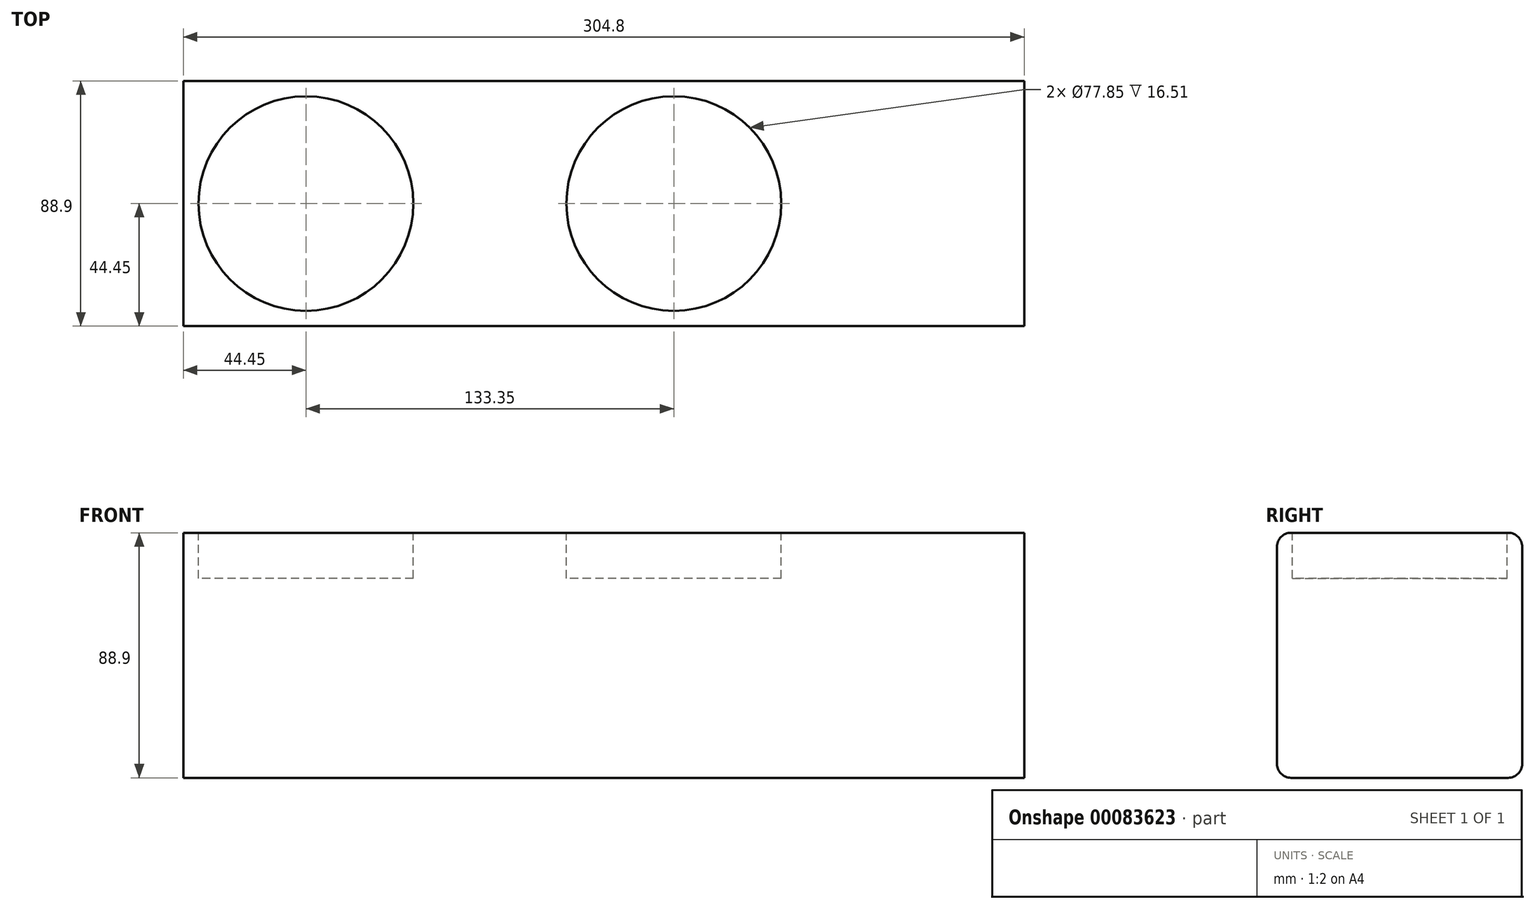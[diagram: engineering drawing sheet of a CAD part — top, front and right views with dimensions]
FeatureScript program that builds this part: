
annotation { "Feature Type Name" : "Feature", "Feature Type Description" : "" }
export const myFeature = defineFeature(function(context is Context, id is Id, definition is map)
    precondition{}
    {
        {
            var Q0;
            Q0=qCreatedBy(makeId("Right.planeOp"),FACE);
            var sketch = newSketch(context, id + "F0", { "sketchPlane" : qUnion([Q0])});
            skLineSegment(sketch, "E0.bottom", {"start": v(44.45, -44.45) * mm, "end": v(-44.45, -44.45) * mm});
            skLineSegment(sketch, "E0.top", {"start": v(44.45, 44.45) * mm, "end": v(-44.45, 44.45) * mm});
            skLineSegment(sketch, "E0.left", {"start": v(44.45, -44.45) * mm, "end": v(44.45, 44.45) * mm});
            skLineSegment(sketch, "E0.right", {"start": v(-44.45, -44.45) * mm, "end": v(-44.45, 44.45) * mm});
            skPoint(sketch, "E0.middle", {"position": v(0, 0) * mm});
            skPoint(sketch, "E1.visualSharp", {"position": v(44.45, -44.45) * mm});
            skPoint(sketch, "E2.visualSharp", {"position": v(44.45, 44.45) * mm});
            skPoint(sketch, "E3.visualSharp", {"position": v(-44.45, 44.45) * mm});
            skPoint(sketch, "E4.visualSharp", {"position": v(-44.45, -44.45) * mm});
            skSolve(sketch);
        }
        {
            var Q0;
            Q0 = qSketchRegion(id + "F0", true);
            extrude(context, id + "F1", {"entities" : qUnion([Q0]), "depth" : 152.4 * mm, "hasSecondDirection" : true, "secondDirectionOppositeDirection" : true, "secondDirectionDepth" : 152.4 * mm});
        }
        {
            var Q0;
            Q0=makeQuery(id+"F1.opExtrude","SWEPT_FACE",FACE,{"disambiguationData":[OSD([sQuery(id+"F0.wireOp",EDGE,"E0.top")])]});
            var sketch = newSketch(context, id + "F2", { "sketchPlane" : qUnion([Q0])});
            skCircle(sketch, "E5", {"center": v(-107.95, 0) * mm, "radius": 38.93 * mm});
            skCircle(sketch, "E6", {"center": v(25.4, 0) * mm, "radius": 38.93 * mm});
            skSolve(sketch);
        }
        {
            var Q0;
            {var subQ0=sQuery(id+"F2.wireOp",EDGE,"E6");var subQ1=sQuery(id+"F0.wireOp",EDGE,"E0.top");var subQ2=makeQuery(id+"F1.opExtrude","SWEPT_EDGE",EDGE,{"disambiguationData":[OSD([subQ1,sQuery(id+"F0.wireOp",EDGE,"E2.filletArc")])]});var subQ3=makeQuery(id+"F2.imprint","INTERSECT",VERTEX,{"disambiguationData":[OD(0.0)],"derivedFrom":[subQ2,subQ0]});Q0=makeQuery(id+"F2.imprint","IMPRINT",FACE,{"disambiguationData":[TD([[makeQuery(id+"F2.imprint","IMPRINT",EDGE,{"disambiguationData":[TD([[subQ3,-1.0]])],"derivedFrom":subQ0}),1.0]])]});}
            var Q1;
            {var subQ0=sQuery(id+"F2.wireOp",EDGE,"E5");var subQ1=sQuery(id+"F0.wireOp",EDGE,"E0.top");var subQ2=makeQuery(id+"F1.opExtrude","SWEPT_EDGE",EDGE,{"disambiguationData":[OSD([subQ1,sQuery(id+"F0.wireOp",EDGE,"E2.filletArc")])]});var subQ3=makeQuery(id+"F2.imprint","INTERSECT",VERTEX,{"disambiguationData":[OD(0.0)],"derivedFrom":[subQ2,subQ0]});Q1=makeQuery(id+"F2.imprint","IMPRINT",FACE,{"disambiguationData":[TD([[makeQuery(id+"F2.imprint","IMPRINT",EDGE,{"disambiguationData":[TD([[subQ3,-1.0]])],"derivedFrom":subQ0}),1.0]])]});}
            extrude(context, id + "F3", {"entities" : qUnion([Q0, Q1]), "operationType" : NewBodyOperationType.REMOVE, "oppositeDirection" : true, "depth" : 16.5 * mm});
        }
        {
            var Q0;
            Q0=makeQuery(id+"F1.opExtrude","SWEPT_EDGE",EDGE,{"disambiguationData":[OSD([sQuery(id+"F0.wireOp",EDGE,"E0.top"),sQuery(id+"F0.wireOp",EDGE,"E0.right")])]});
            var Q1;
            Q1=makeQuery(id+"F1.opExtrude","SWEPT_EDGE",EDGE,{"disambiguationData":[OSD([sQuery(id+"F0.wireOp",EDGE,"E0.top"),sQuery(id+"F0.wireOp",EDGE,"E0.left")])]});
            var Q2;
            Q2=makeQuery(id+"F1.opExtrude","SWEPT_EDGE",EDGE,{"disambiguationData":[OSD([sQuery(id+"F0.wireOp",EDGE,"E0.bottom"),sQuery(id+"F0.wireOp",EDGE,"E0.right")])]});
            var Q3;
            Q3=makeQuery(id+"F1.opExtrude","SWEPT_EDGE",EDGE,{"disambiguationData":[OSD([sQuery(id+"F0.wireOp",EDGE,"E0.bottom"),sQuery(id+"F0.wireOp",EDGE,"E0.left")])]});
            fillet(context, id + "F4", {"entities" : qUnion([Q0, Q1, Q2, Q3]), "radius" : 5.08 * mm, "tangentPropagation" : true, "allowEdgeOverflow" : false});
        }
    });
